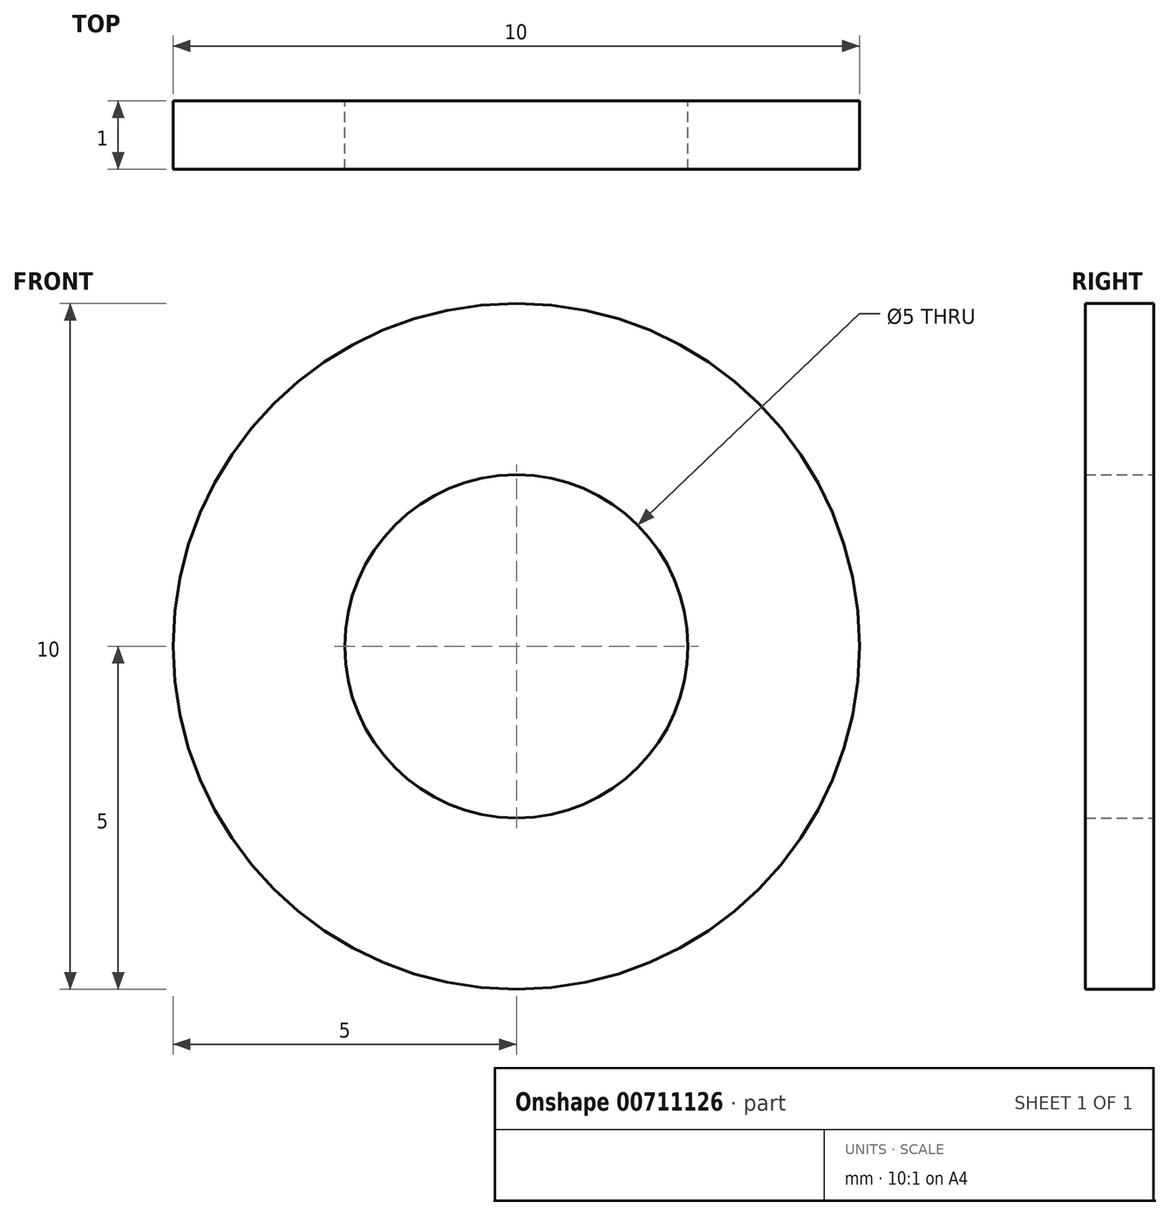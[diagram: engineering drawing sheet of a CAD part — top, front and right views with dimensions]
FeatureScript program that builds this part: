
annotation { "Feature Type Name" : "Feature", "Feature Type Description" : "" }
export const myFeature = defineFeature(function(context is Context, id is Id, definition is map)
    precondition{}
    {
        {
            var Q0;
            Q0=qCreatedBy(makeId("Front.planeOp"),FACE);
            var sketch = newSketch(context, id + "F0", { "sketchPlane" : qUnion([Q0])});
            skCircle(sketch, "E0", {"center": v(0, 0) * mm, "radius": 5 * mm});
            skCircle(sketch, "E1", {"center": v(0, 0) * mm, "radius": 2.5 * mm});
            skSolve(sketch);
        }
        {
            var Q0;
            Q0 = qSketchRegion(id + "F0", true);
            extrude(context, id + "F1", {"entities" : qUnion([Q0]), "depth" : 1 * mm, "offsetDistance" : 25 * mm});
        }
    });
